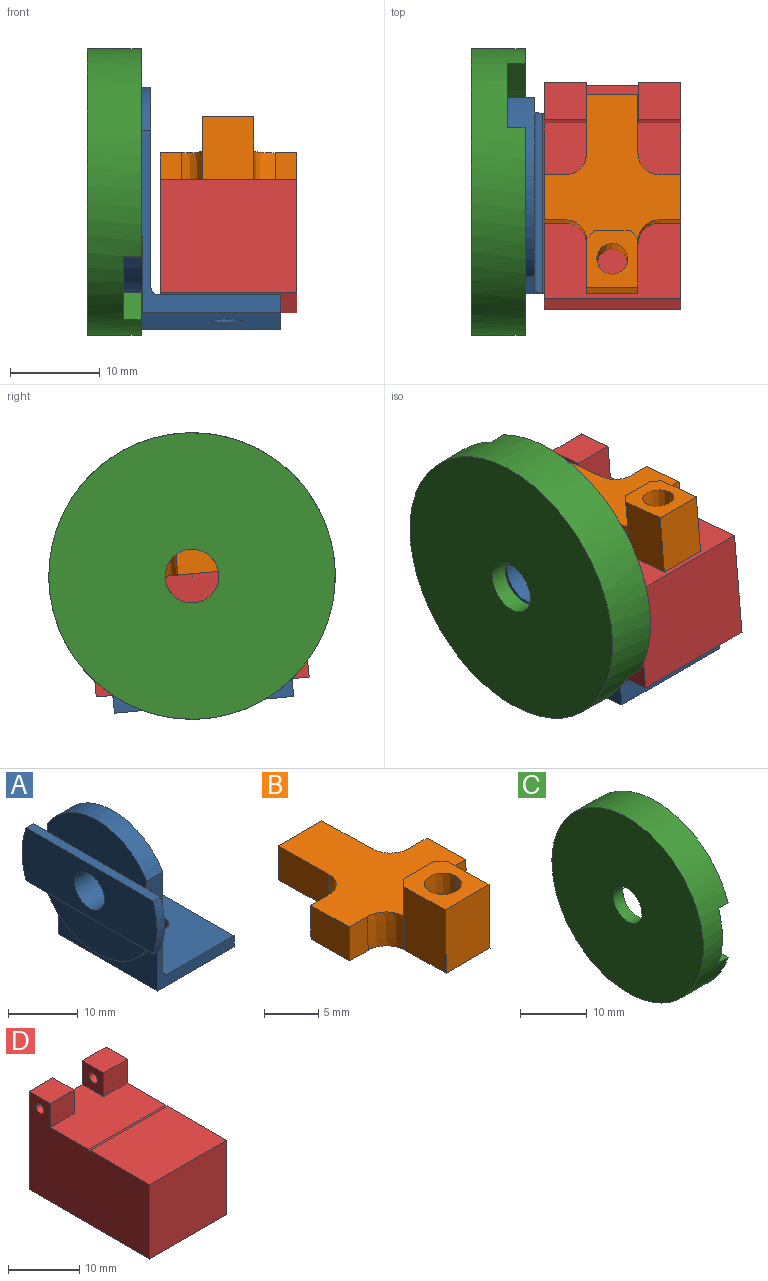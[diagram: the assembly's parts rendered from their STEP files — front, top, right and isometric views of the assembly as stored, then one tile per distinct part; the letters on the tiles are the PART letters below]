
ASSEMBLY  parts=4 mates=3
PART A: 23 faces, bbox 19.2x27.4x26.2 mm
  f0: plane 20.1x7.05mm, normal (-1,0,0), area 108.2mm2, adj f1,f3,f4,f12
  f1: plane 20.44x17.73mm, normal (0,1,0), area 69.6mm2, adj f0,f2,f4,f6,f7,f8,f10,f12
  f2: cylinder r=11.7mm len=20.1mm, axis (1,0,0), area 79.8mm2, adj f1,f3,f6,f7
  f3: plane 20.44x17.73mm, normal (0,-1,0), area 69.6mm2, adj f0,f2,f4,f6,f7,f8,f10,f12
  f4: cylinder r=11.7mm len=20.1mm, axis (1,0,0), area 55.6mm2, adj f0,f1,f3,f8
  f5: cylinder r=3mm len=6mm, axis (1,0,0), area 90.5mm2, adj f7,f14
  f6: plane 20.1x7.05mm, normal (-1,0,0), area 108.2mm2, adj f1,f2,f3,f10
  f7: plane 23.35x20.1mm, normal (1,0,0), area 407.5mm2, adj f1,f2,f3,f5,f22
  f8: plane 20.1x8.46mm, normal (-1,0,0), area 88.8mm2, adj f1,f3,f4,f17
  f9: plane 9.3x2.85mm, normal (1,0,0), area 24mm2, adj f10,f11,f12,f21
  f10: plane 25.77x2.3mm, normal (0,0,1), area 38.9mm2, adj f1,f3,f6,f9,f11,f13,f14,f15
  f11: cylinder r=13.7mm len=9.3mm, axis (1,0,0), area 14.2mm2, adj f9,f10,f12,f14
  f12: plane 25.77x2.3mm, normal (0,0,-1), area 38.9mm2, adj f0,f1,f3,f9,f11,f13,f14,f15
  f13: cylinder r=13.7mm len=9.3mm, axis (1,0,0), area 14.2mm2, adj f10,f12,f14,f15
  f14: plane 27.4x9.3mm, normal (-1,0,0), area 221.6mm2, adj f5,f10,f11,f12,f13
  f15: plane 9.3x2.85mm, normal (1,0,0), area 24mm2, adj f10,f12,f13,f20
  f16: plane 20.1x2mm, normal (1,0,0), area 40.2mm2, adj f1,f3,f17,f18
  f17: plane 20.1x15.43mm, normal (0,0,-1), area 299.7mm2, adj f1,f3,f8,f16,f19
  f18: plane 20.1x13.63mm, normal (0,0,1), area 263.5mm2, adj f1,f3,f16,f19,f22
  f19: cylinder r=1.83mm len=3.66mm, axis (0,0,1), area 23mm2, adj f17,f18
  f20: cylinder r=0.8mm len=9.3mm, axis (0,0,-1), area 11.7mm2, adj f3,f10,f12,f15
  f21: cylinder r=0.8mm len=9.3mm, axis (0,0,1), area 11.7mm2, adj f1,f9,f10,f12
  f22: cylinder r=0.8mm len=20.1mm, axis (0,1,0), area 25.3mm2, adj f1,f3,f7,f18
PART B: 24 faces, bbox 15.2x22x7.5 mm
  f0: plane 21.95x15.24mm, normal (0,-0.02,-1), area 169.3mm2, adj f1,f2,f3,f4,f5,f6,f7,f8
  f1: extruded ~3.85x2.45mm, area 14.2mm2, adj f0,f2,f14,f19
  f2: plane 3.81x2.38mm, normal (0,-1,0.02), area 9.1mm2, adj f0,f1,f3,f14
  f3: plane 5.15x3.9mm, normal (1,0,0), area 19.4mm2, adj f0,f2,f4,f14
  f4: plane 3.81x2.38mm, normal (0,1,-0.02), area 9.1mm2, adj f0,f3,f5,f14
  f5: extruded ~3.85x2.45mm, area 14.2mm2, adj f0,f4,f6,f14
  f6: plane 6.7x3.93mm, normal (1,0,0), area 25.3mm2, adj f0,f5,f7,f14
  f7: plane 5.72x3.81mm, normal (0,1,-0.02), area 21.8mm2, adj f0,f6,f8,f14
  f8: plane 6.7x3.93mm, normal (-1,0,0), area 25.3mm2, adj f0,f7,f9,f14
  f9: extruded ~3.85x2.45mm, area 14.2mm2, adj f0,f8,f10,f14
  f10: plane 3.81x2.38mm, normal (0,1,-0.02), area 9.1mm2, adj f0,f9,f11,f14
  f11: plane 5.15x3.9mm, normal (-1,0,0), area 19.4mm2, adj f0,f10,f12,f14
  f12: plane 3.81x2.38mm, normal (0,-1,0.02), area 9.1mm2, adj f0,f11,f13,f14
  f13: extruded ~3.85x2.45mm, area 14.2mm2, adj f0,f12,f14,f17
  f14: plane 16.48x15.24mm, normal (0,0.02,1), area 143.2mm2, adj f1,f2,f3,f4,f5,f6,f7,f8
  f15: plane 3.96x3.3mm, normal (0,1,-0.02), area 13.1mm2, adj f14,f16,f22,f23
  f16: plane 3.32x0.94mm, normal (-0.71,0.71,-0.01), area 4.1mm2, adj f14,f15,f17,f23
  f17: plane 7.21x5.6mm, normal (-1,0,0), area 38.9mm2, adj f0,f13,f16,f18,f23
  f18: plane 7.11x5.72mm, normal (0,-1,0.02), area 40.6mm2, adj f0,f17,f19,f23
  f19: plane 7.21x5.6mm, normal (1,0,0), area 38.9mm2, adj f0,f1,f18,f22,f23
  f20: extruded ~7.14x3.45mm, area 38.6mm2, adj f0,f21,f23
  f21: extruded ~7.14x3.45mm, area 38.6mm2, adj f0,f20,f23
  f22: plane 3.32x0.94mm, normal (0.71,0.71,-0.01), area 4.1mm2, adj f14,f15,f19,f23
  f23: plane 6.35x5.72mm, normal (0,0.02,1), area 26.1mm2, adj f15,f16,f17,f18,f19,f20,f21,f22
PART C: 17 faces, bbox 6x32x32 mm
  f0: cylinder r=12mm len=21.82mm, axis (-1,0,0), area 54.8mm2, adj f1,f2,f4,f15
  f1: plane 30.4x11mm, normal (1,0,0), area 135mm2, adj f0,f4,f8,f15
  f2: plane 26.15x9mm, normal (-1,0,0), area 61.1mm2, adj f0,f4,f11,f15
  f3: plane 4.29x2mm, normal (0,0,1), area 8.6mm2, adj f5,f6,f8,f12,f13
  f4: plane 4.29x2mm, normal (0,0,-1), area 8.6mm2, adj f0,f1,f2,f5,f8
  f5: plane 10x2.92mm, normal (1,0,0), area 20.4mm2, adj f3,f4,f8,f11
  f6: plane 30.4x11mm, normal (1,0,0), area 135mm2, adj f3,f8,f12,f16
  f7: plane 28x28mm, normal (1,0,0), area 587.5mm2, adj f9,f11
  f8: cylinder r=16mm len=32mm, axis (1,0,0), area 562.5mm2, adj f1,f3,f4,f5,f6,f10,f14,f15
  f9: cylinder r=3mm len=6mm, axis (1,0,0), area 37.7mm2, adj f7,f10
  f10: plane 32x32mm, normal (-1,0,0), area 776mm2, adj f8,f9
  f11: cylinder r=14mm len=28mm, axis (-1,0,0), area 175.9mm2, adj f2,f5,f7,f13,f14
  f12: cylinder r=12mm len=21.82mm, axis (-1,0,0), area 54.8mm2, adj f3,f6,f13,f16
  f13: plane 26.15x9mm, normal (-1,0,0), area 61.1mm2, adj f3,f11,f12,f16
  f14: plane 10x2.92mm, normal (1,0,0), area 20.4mm2, adj f8,f11,f15,f16
  f15: plane 4.29x2mm, normal (0,0,-1), area 8.6mm2, adj f0,f1,f2,f8,f14
  f16: plane 4.29x2mm, normal (0,0,1), area 8.6mm2, adj f6,f8,f12,f13,f14
PART D: 17 faces, bbox 15.2x23.9x16.8 mm
  f0: plane 4.19x4.07mm, normal (1,0,0), area 15.1mm2, adj f2,f3,f4,f8,f15
  f1: plane 4.19x4.07mm, normal (-1,0,0), area 15.1mm2, adj f5,f6,f8,f9,f15
  f2: cylinder r=0.79mm len=4.7mm, axis (-1,0,0), area 23.2mm2, adj f0,f10
  f3: plane 4.7x4.19mm, normal (0,0,1), area 19.7mm2, adj f0,f4,f10,f15
  f4: plane 4.7x4.06mm, normal (0,-1,0), area 19.1mm2, adj f0,f3,f8,f10
  f5: plane 4.7x4.06mm, normal (0,-1,0), area 19.1mm2, adj f1,f6,f8,f12
  f6: plane 4.7x4.19mm, normal (0,0,1), area 19.7mm2, adj f1,f5,f12,f15
  f7: plane 15.24x0.25mm, normal (0,-0.87,0.5), area 4.4mm2, adj f8,f10,f11,f12
  f8: plane 15.24x11.77mm, normal (0,0,1), area 140mm2, adj f0,f1,f4,f5,f7,f10,f12,f15
  f9: cylinder r=0.79mm len=4.7mm, axis (-1,0,0), area 23.2mm2, adj f1,f12
  f10: plane 23.88x16.77mm, normal (-1,0,0), area 318.3mm2, adj f2,f3,f4,f7,f8,f11,f13,f14
  f11: plane 15.24x0.25mm, normal (0,0.86,0.51), area 4.4mm2, adj f7,f10,f12,f14
  f12: plane 23.88x16.77mm, normal (1,0,0), area 318.3mm2, adj f5,f6,f7,f8,f9,f11,f13,f14
  f13: plane 15.24x12.7mm, normal (0,-1,0), area 193.5mm2, adj f10,f12,f14,f16
  f14: plane 15.24x11.82mm, normal (0,0,1), area 180.1mm2, adj f10,f11,f12,f13
  f15: plane 16.76x15.24mm, normal (0,1,0), area 231.7mm2, adj f0,f1,f3,f6,f8,f10,f12,f16
  f16: plane 23.88x15.24mm, normal (0,0,-1), area 363.9mm2, adj f10,f12,f13,f15
PLACE A rot(axis=(-1,0,0),5.4deg) t=(6.82,10.74,-12.58)mm
PLACE B rot(axis=(-1,0,0),4.3deg) t=(6.78,10.03,-12.73)mm
PLACE C rot(axis=(1,0,0),45deg) t=(6.72,16.54,0.25)mm
PLACE D rot(axis=(-1,0,0),5.4deg) t=(6.84,10.74,-12.58)mm
MATE fastened D.f16 <-> A.f19  axis (0,-0.09,-1) through (15.74,-1.19,-12.39)mm
MATE cylindrical A.f2 <-> C.f0  axis (-1,0,0) through (2.3,0,0)mm
MATE fastened B.f0 <-> D.f14  axis (0,-0.09,-1) through (15.74,-0.12,0.26)mm
